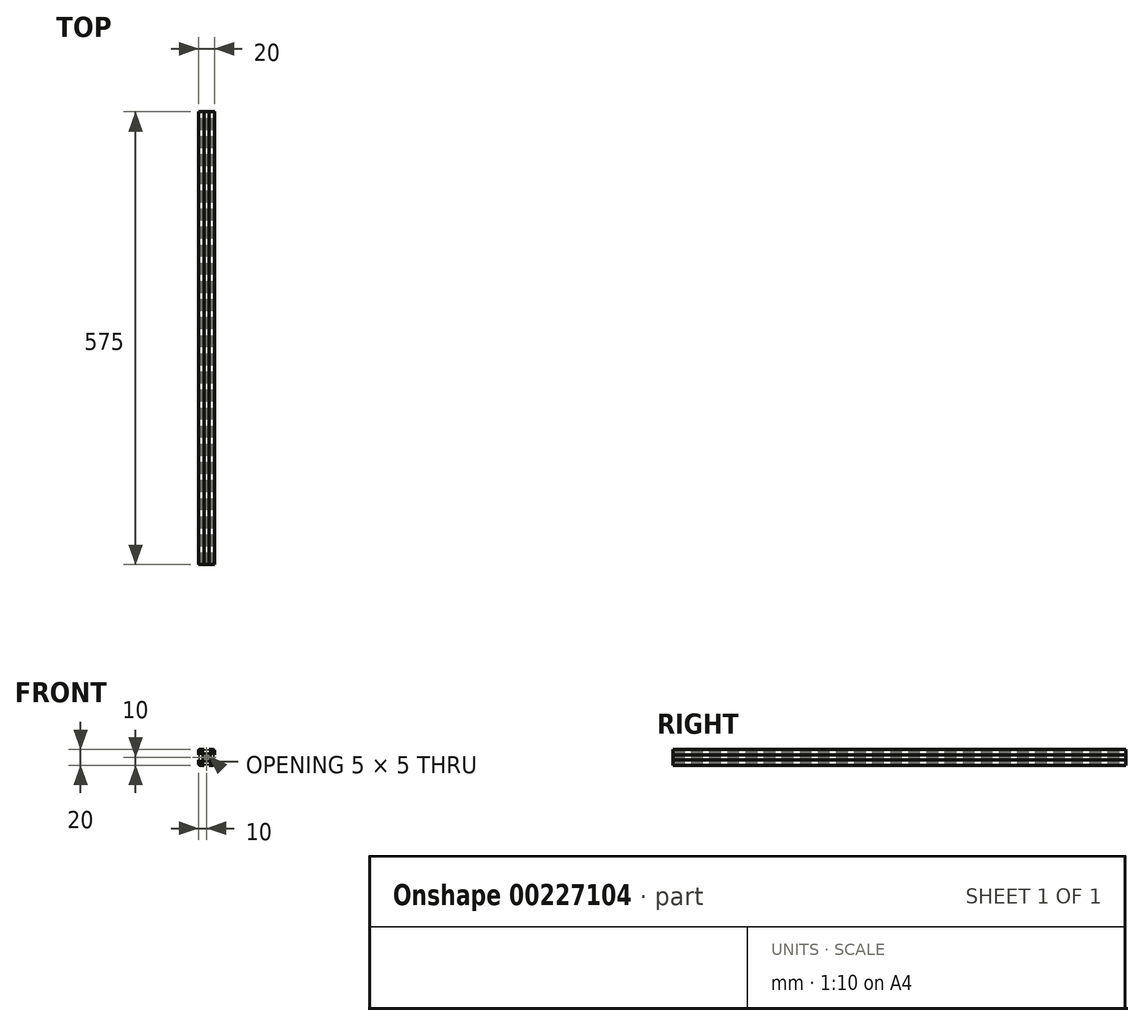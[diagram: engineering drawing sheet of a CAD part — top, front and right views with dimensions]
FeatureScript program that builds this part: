
annotation { "Feature Type Name" : "Feature", "Feature Type Description" : "" }
export const myFeature = defineFeature(function(context is Context, id is Id, definition is map)
    precondition{}
    {
        {
            var Q0;
            Q0=qCreatedBy(makeId("Front.planeOp"),FACE);
            var sketch = newSketch(context, id + "F0", { "sketchPlane" : qUnion([Q0])});
            skLineSegment(sketch, "E0.bottom", {"start": v(8.5, -10) * mm, "end": v(3, -10) * mm});
            skLineSegment(sketch, "E0.top", {"start": v(8.5, 10) * mm, "end": v(3, 10) * mm});
            skLineSegment(sketch, "E0.left", {"start": v(10, -8.5) * mm, "end": v(10, -3) * mm});
            skLineSegment(sketch, "E0.right", {"start": v(-10, -8.5) * mm, "end": v(-10, -3) * mm});
            skPoint(sketch, "E0.middle", {"position": v(0, 0) * mm});
            skLineSegment(sketch, "E1.bottom", {"start": v(6, -8.5) * mm, "end": v(3, -8.5) * mm});
            skLineSegment(sketch, "E1.top", {"start": v(6, 8.5) * mm, "end": v(3, 8.5) * mm});
            skLineSegment(sketch, "E1.left", {"start": v(8.5, -6) * mm, "end": v(8.5, -3) * mm});
            skLineSegment(sketch, "E1.right", {"start": v(-8.5, -6) * mm, "end": v(-8.5, -3) * mm});
            skLineSegment(sketch, "E2.bottom", {"start": v(3.44, -4.5) * mm, "end": v(-3.44, -4.5) * mm});
            skLineSegment(sketch, "E2.top", {"start": v(3.44, 4.5) * mm, "end": v(-3.44, 4.5) * mm});
            skLineSegment(sketch, "E2.left", {"start": v(4.5, -3.44) * mm, "end": v(4.5, 3.44) * mm});
            skLineSegment(sketch, "E2.right", {"start": v(-4.5, -3.44) * mm, "end": v(-4.5, 3.44) * mm});
            skLineSegment(sketch, "E3.bottom", {"start": v(8.5, -6) * mm, "end": v(7.06, -6) * mm});
            skLineSegment(sketch, "E3.top", {"start": v(8.5, 6) * mm, "end": v(7.06, 6) * mm});
            skLineSegment(sketch, "E4.left", {"start": v(6, -8.5) * mm, "end": v(6, -7.06) * mm});
            skLineSegment(sketch, "E4.right", {"start": v(-6, -8.5) * mm, "end": v(-6, -7.06) * mm});
            skPoint(sketch, "E5.orphan", {"position": v(-8.5, 8.5) * mm});
            skPoint(sketch, "E6.orphan", {"position": v(8.5, 8.5) * mm});
            skPoint(sketch, "E7.orphan", {"position": v(8.5, -8.5) * mm});
            skPoint(sketch, "E8.orphan", {"position": v(-8.5, -8.5) * mm});
            skLineSegment(sketch, "E9.trimOffspring", {"start": v(-6, 7.06) * mm, "end": v(-6, 8.5) * mm});
            skLineSegment(sketch, "E10.trimOffspring", {"start": v(-7.06, 6) * mm, "end": v(-8.5, 6) * mm});
            skLineSegment(sketch, "E11.trimOffspring", {"start": v(6, 7.06) * mm, "end": v(6, 8.5) * mm});
            skLineSegment(sketch, "E12.trimOffspring", {"start": v(-7.06, -6) * mm, "end": v(-8.5, -6) * mm});
            skLineSegment(sketch, "E13", {"start": v(-10, 10) * mm, "end": v(0, 0) * mm, "construction": true});
            skLineSegment(sketch, "E14", {"start": v(10, 10) * mm, "end": v(0, 0) * mm, "construction": true});
            skLineSegment(sketch, "E15", {"start": v(-6, 7.06) * mm, "end": v(-3.44, 4.5) * mm});
            skPoint(sketch, "E15.endSnap0", {"position": v(7.25, -6) * mm});
            skLineSegment(sketch, "E16", {"start": v(6, -7.06) * mm, "end": v(3.44, -4.5) * mm});
            skLineSegment(sketch, "E17", {"start": v(7.06, 6) * mm, "end": v(4.5, 3.44) * mm});
            skLineSegment(sketch, "E18", {"start": v(6, 7.06) * mm, "end": v(3.44, 4.5) * mm});
            skPoint(sketch, "E19.orphan", {"position": v(6, -6) * mm});
            skPoint(sketch, "E20.orphan", {"position": v(-4.5, -4.5) * mm});
            skPoint(sketch, "E21.orphan", {"position": v(-4.5, 4.5) * mm});
            skPoint(sketch, "E22.orphan", {"position": v(4.5, 4.5) * mm});
            skPoint(sketch, "E23.orphan", {"position": v(4.5, -4.5) * mm});
            skLineSegment(sketch, "E24.trimOffspring", {"start": v(4.5, -3.44) * mm, "end": v(7.06, -6) * mm});
            skLineSegment(sketch, "E25.trimOffspring", {"start": v(-3.44, -4.5) * mm, "end": v(-6, -7.06) * mm});
            skLineSegment(sketch, "E26.trimOffspring", {"start": v(-4.5, -3.44) * mm, "end": v(-7.06, -6) * mm});
            skLineSegment(sketch, "E27.trimOffspring", {"start": v(-4.5, 3.44) * mm, "end": v(-7.06, 6) * mm});
            skLineSegment(sketch, "E28.bottom", {"start": v(8.5, -3) * mm, "end": v(10, -3) * mm});
            skLineSegment(sketch, "E28.top", {"start": v(8.5, 3) * mm, "end": v(10, 3) * mm});
            skPoint(sketch, "E28.middle", {"position": v(10, 0) * mm});
            skLineSegment(sketch, "E29.left", {"start": v(3, 8.5) * mm, "end": v(3, 10) * mm});
            skLineSegment(sketch, "E29.right", {"start": v(-3, 8.5) * mm, "end": v(-3, 10) * mm});
            skPoint(sketch, "E29.middle", {"position": v(0, 10) * mm});
            skLineSegment(sketch, "E30.bottom", {"start": v(-8.5, 3) * mm, "end": v(-10, 3) * mm});
            skLineSegment(sketch, "E30.top", {"start": v(-8.5, -3) * mm, "end": v(-10, -3) * mm});
            skPoint(sketch, "E30.middle", {"position": v(-10, 0) * mm});
            skLineSegment(sketch, "E31.left", {"start": v(3, -8.5) * mm, "end": v(3, -10) * mm});
            skLineSegment(sketch, "E31.right", {"start": v(-3, -8.5) * mm, "end": v(-3, -10) * mm});
            skPoint(sketch, "E31.middle", {"position": v(0, -10) * mm});
            skPoint(sketch, "E32.orphan", {"position": v(3, 11.5) * mm});
            skPoint(sketch, "E33.orphan", {"position": v(-3, 11.5) * mm});
            skLineSegment(sketch, "E34.trimOffspring", {"start": v(-3, 10) * mm, "end": v(-8.5, 10) * mm});
            skLineSegment(sketch, "E35.trimOffspring", {"start": v(-3, 8.5) * mm, "end": v(-6, 8.5) * mm});
            skPoint(sketch, "E28.right.end.orphan", {"position": v(11.5, 3) * mm});
            skPoint(sketch, "E36.orphan", {"position": v(11.5, -3) * mm});
            skLineSegment(sketch, "E37.trimOffspring", {"start": v(10, 3) * mm, "end": v(10, 8.5) * mm});
            skLineSegment(sketch, "E38.trimOffspring", {"start": v(8.5, 3) * mm, "end": v(8.5, 6) * mm});
            skPoint(sketch, "E39.orphan", {"position": v(3, -11.5) * mm});
            skPoint(sketch, "E40.orphan", {"position": v(-3, -11.5) * mm});
            skLineSegment(sketch, "E41.trimOffspring", {"start": v(-3, -10) * mm, "end": v(-8.5, -10) * mm});
            skLineSegment(sketch, "E42.trimOffspring", {"start": v(-3, -8.5) * mm, "end": v(-6, -8.5) * mm});
            skPoint(sketch, "E30.right.end.orphan", {"position": v(-11.5, -3) * mm});
            skPoint(sketch, "E43.orphan", {"position": v(-11.5, 3) * mm});
            skLineSegment(sketch, "E44.trimOffspring", {"start": v(-10, 3) * mm, "end": v(-10, 8.5) * mm});
            skLineSegment(sketch, "E45.trimOffspring", {"start": v(-8.5, 3) * mm, "end": v(-8.5, 6) * mm});
            skLineSegment(sketch, "E46.trimOffspring", {"start": v(0, 0) * mm, "end": v(10, -10) * mm, "construction": true});
            skLineSegment(sketch, "E47.trimOffspring", {"start": v(0, 0) * mm, "end": v(-10, -10) * mm, "construction": true});
            skArc(sketch, "E48", {"start": v(1.16, 2.22) * mm, "mid": v(0, 2.5) * mm, "end": v(-1.16, 2.22) * mm});
            skLineSegment(sketch, "E49", {"start": v(-2.5, -1.44) * mm, "end": v(1.44, 2.5) * mm});
            skLineSegment(sketch, "E50", {"start": v(2.5, 1.44) * mm, "end": v(-1.44, -2.5) * mm});
            skLineSegment(sketch, "E51", {"start": v(1.44, -2.5) * mm, "end": v(-2.5, 1.44) * mm});
            skLineSegment(sketch, "E52", {"start": v(-1.44, 2.5) * mm, "end": v(2.5, -1.44) * mm});
            skLineSegment(sketch, "E53", {"start": v(2.5, 1.44) * mm, "end": v(2.5, -1.44) * mm, "construction": true});
            skLineSegment(sketch, "E54", {"start": v(1.44, -2.5) * mm, "end": v(-1.44, -2.5) * mm, "construction": true});
            skLineSegment(sketch, "E55", {"start": v(-2.5, -1.44) * mm, "end": v(-2.5, 1.44) * mm, "construction": true});
            skLineSegment(sketch, "E56", {"start": v(-1.44, 2.5) * mm, "end": v(1.44, 2.5) * mm, "construction": true});
            skLineSegment(sketch, "E57", {"start": v(-1.44, 2.5) * mm, "end": v(-2.5, 1.44) * mm});
            skLineSegment(sketch, "E58", {"start": v(1.44, 2.5) * mm, "end": v(2.5, 1.44) * mm});
            skLineSegment(sketch, "E59", {"start": v(2.5, -1.44) * mm, "end": v(1.44, -2.5) * mm});
            skLineSegment(sketch, "E60", {"start": v(-1.44, -2.5) * mm, "end": v(-2.5, -1.44) * mm});
            skArc(sketch, "E61.trimOffspring", {"start": v(-2.22, 1.16) * mm, "mid": v(-2.5, 0) * mm, "end": v(-2.22, -1.16) * mm});
            skArc(sketch, "E62.trimOffspring", {"start": v(-1.16, -2.22) * mm, "mid": v(0, -2.5) * mm, "end": v(1.16, -2.22) * mm});
            skArc(sketch, "E63.trimOffspring", {"start": v(2.22, -1.16) * mm, "mid": v(2.5, 0) * mm, "end": v(2.22, 1.16) * mm});
            skPoint(sketch, "E64.visualSharp", {"position": v(10, 10) * mm});
            skArc(sketch, "E64.filletArc", {"start": v(10, 8.5) * mm, "mid": v(9.56, 9.56) * mm, "end": v(8.5, 10) * mm});
            skPoint(sketch, "E65.visualSharp", {"position": v(10, -10) * mm});
            skArc(sketch, "E65.filletArc", {"start": v(8.5, -10) * mm, "mid": v(9.56, -9.56) * mm, "end": v(10, -8.5) * mm});
            skPoint(sketch, "E66.visualSharp", {"position": v(-10, -10) * mm});
            skArc(sketch, "E66.filletArc", {"start": v(-10, -8.5) * mm, "mid": v(-9.56, -9.56) * mm, "end": v(-8.5, -10) * mm});
            skPoint(sketch, "E67.visualSharp", {"position": v(-10, 10) * mm});
            skArc(sketch, "E67.filletArc", {"start": v(-8.5, 10) * mm, "mid": v(-9.56, 9.56) * mm, "end": v(-10, 8.5) * mm});
            skSolve(sketch);
        }
        {
            assignVariable(context, id + "F2", {"name" : "Length", "anyValue" : 575});
        }
        {
            var Q0;
            Q0=qSketchRegion(id+"F0",true);
            extrude(context, id + "F1", {"entities" : qUnion([Q0]), "depth" : (getVariable(context, 'Length')) * mm});
        }
    });
